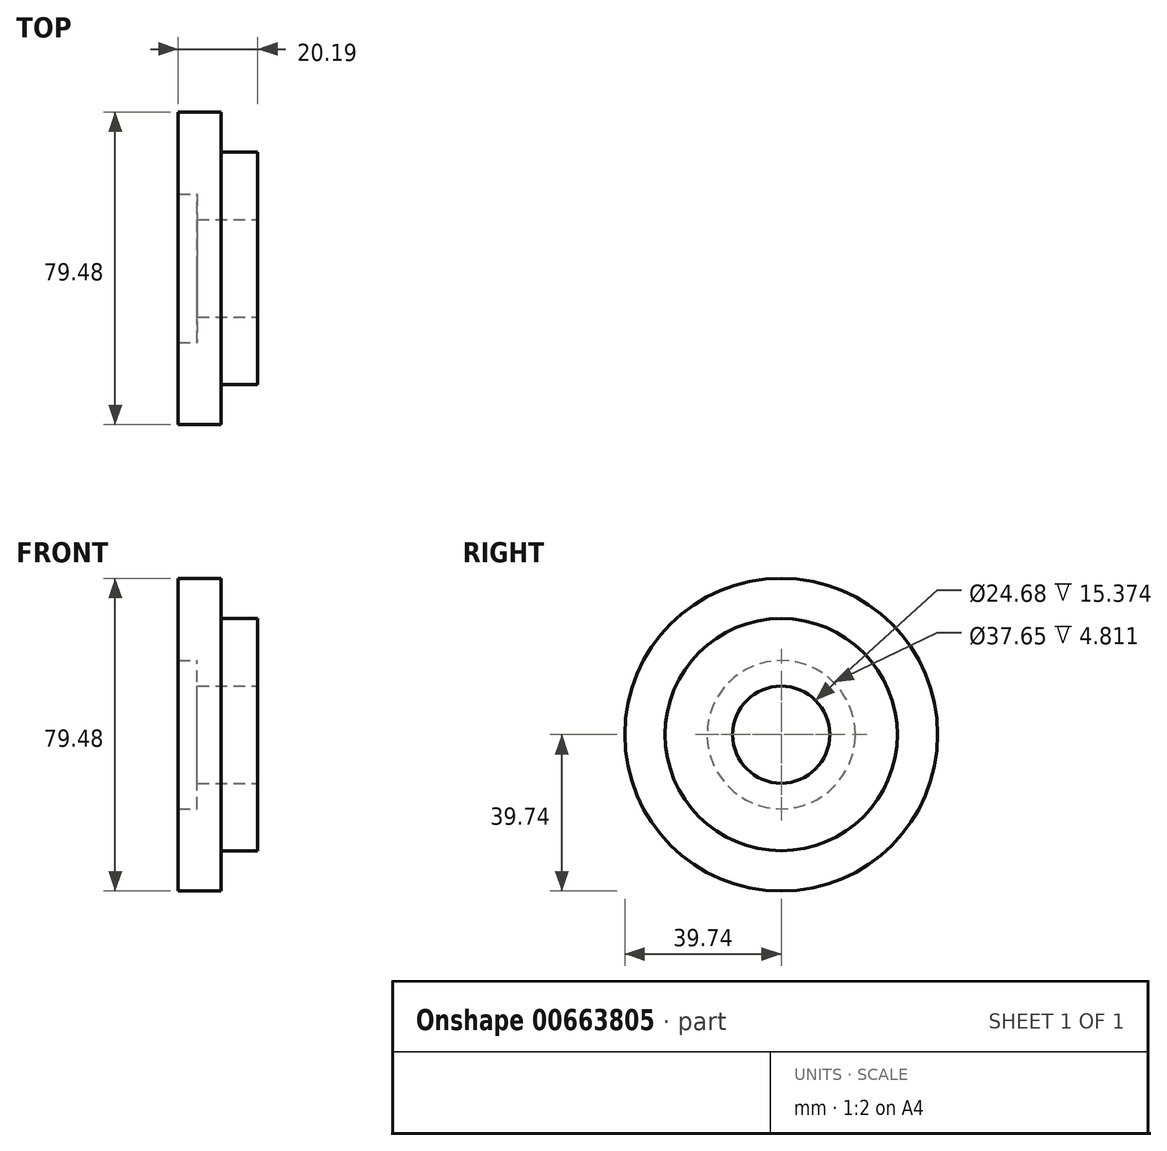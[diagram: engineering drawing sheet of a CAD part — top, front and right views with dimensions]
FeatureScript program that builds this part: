
annotation { "Feature Type Name" : "Feature", "Feature Type Description" : "" }
export const myFeature = defineFeature(function(context is Context, id is Id, definition is map)
    precondition{}
    {
        {
            var Q0;
            Q0=qCreatedBy(makeId("Front.planeOp"),FACE);
            var sketch = newSketch(context, id + "F0", { "sketchPlane" : qUnion([Q0])});
            skLineSegment(sketch, "E0", {"start": v(0, 12.34) * mm, "end": v(0, 29.5) * mm});
            skLineSegment(sketch, "E1", {"start": v(0, 29.5) * mm, "end": v(-9.3, 29.5) * mm});
            skLineSegment(sketch, "E2", {"start": v(-9.3, 29.5) * mm, "end": v(-9.3, 39.74) * mm});
            skLineSegment(sketch, "E3", {"start": v(-9.3, 39.74) * mm, "end": v(-20.19, 39.74) * mm});
            skLineSegment(sketch, "E4", {"start": v(-20.19, 39.74) * mm, "end": v(-20.19, 18.83) * mm});
            skLineSegment(sketch, "E5", {"start": v(-20.19, 18.83) * mm, "end": v(-15.37, 18.83) * mm});
            skLineSegment(sketch, "E6", {"start": v(-15.37, 18.83) * mm, "end": v(-15.37, 12.34) * mm});
            skLineSegment(sketch, "E7", {"start": v(-15.37, 12.34) * mm, "end": v(0, 12.34) * mm});
            skLineSegment(sketch, "E8", {"start": v(0, 0) * mm, "end": v(-39.01, 0) * mm});
            skSolve(sketch);
        }
        {
            var Q0;
            Q0=makeQuery(id+"F0.imprint","IMPRINT",FACE,{"disambiguationData":[TD([[makeQuery(id+"F0.imprint","IMPRINT",EDGE,{"derivedFrom":sQuery(id+"F0.wireOp",EDGE,"E0")}),1.0]])]});
            var Q1;
            Q1=sQuery(id+"F0.wireOp",EDGE,"E8");
            revolve(context, id + "F1", {"entities" : qUnion([Q0]), "axis" : qUnion([Q1]), "revolveType" : RevolveType.FULL});
        }
    });
